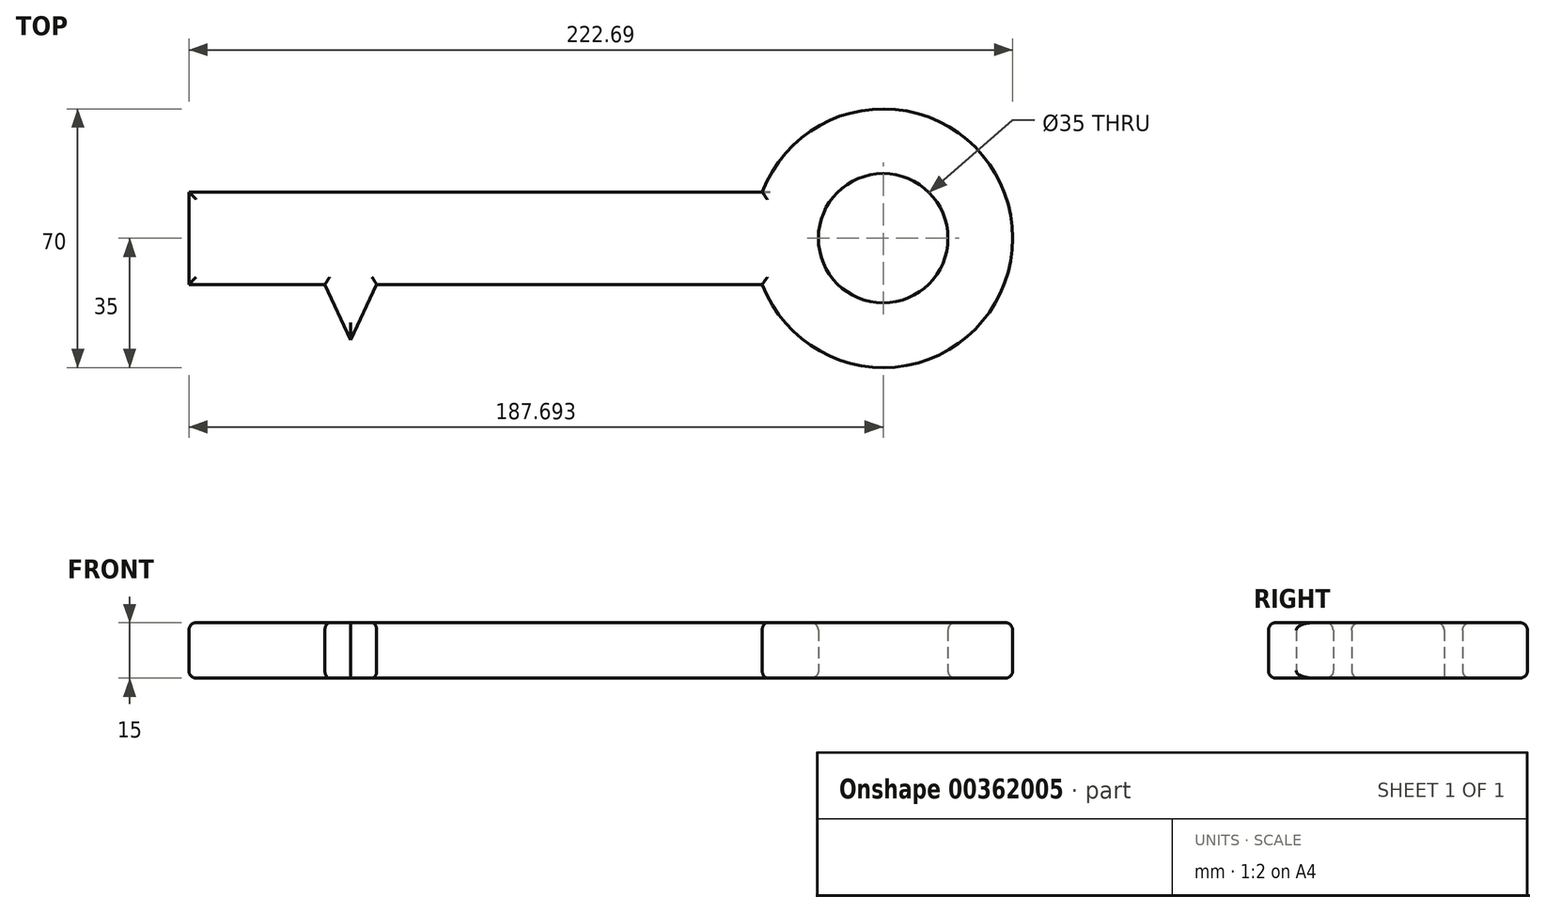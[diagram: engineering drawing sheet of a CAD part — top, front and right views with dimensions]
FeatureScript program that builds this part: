
annotation { "Feature Type Name" : "Feature", "Feature Type Description" : "" }
export const myFeature = defineFeature(function(context is Context, id is Id, definition is map)
    precondition{}
    {
        {
            var Q0;
            Q0=qCreatedBy(makeId("Top.planeOp"),FACE);
            var sketch = newSketch(context, id + "F0", { "sketchPlane" : qUnion([Q0])});
            skLineSegment(sketch, "E0.bottom", {"start": v(1.05, 45.74) * mm, "end": v(-153.95, 45.74) * mm});
            skLineSegment(sketch, "E0.top", {"start": v(1.05, 20.74) * mm, "end": v(-153.95, 20.74) * mm});
            skLineSegment(sketch, "E0.left", {"start": v(1.05, 45.74) * mm, "end": v(1.05, 20.74) * mm});
            skLineSegment(sketch, "E0.right", {"start": v(-153.95, 45.74) * mm, "end": v(-153.95, 20.74) * mm});
            skLineSegment(sketch, "E1.bottom", {"start": v(-153.95, 20.74) * mm, "end": v(-153.95, 20.74) * mm});
            skLineSegment(sketch, "E1.top", {"start": v(-153.95, -9.26) * mm, "end": v(-153.95, -9.26) * mm});
            skLineSegment(sketch, "E1.left", {"start": v(-153.95, 20.74) * mm, "end": v(-153.95, -9.26) * mm});
            skLineSegment(sketch, "E1.right", {"start": v(-153.95, 20.74) * mm, "end": v(-153.95, -9.26) * mm});
            skLineSegment(sketch, "E2.bottom", {"start": v(-153.95, -9.26) * mm, "end": v(-144.47, -9.26) * mm});
            skLineSegment(sketch, "E3.bottom", {"start": v(-144.47, -9.26) * mm, "end": v(-144.47, -9.26) * mm});
            skLineSegment(sketch, "E3.top", {"start": v(-144.47, 20.74) * mm, "end": v(-144.47, 20.74) * mm});
            skLineSegment(sketch, "E3.left", {"start": v(-144.47, -9.26) * mm, "end": v(-144.47, 20.74) * mm});
            skLineSegment(sketch, "E3.right", {"start": v(-144.47, -9.26) * mm, "end": v(-144.47, 20.74) * mm});
            skLineSegment(sketch, "E4.bottom", {"start": v(-134.47, 20.74) * mm, "end": v(-135.17, 20.74) * mm});
            skLineSegment(sketch, "E4.top", {"start": v(-134.47, 5.74) * mm, "end": v(-135.17, 5.74) * mm});
            skLineSegment(sketch, "E4.left", {"start": v(-135.17, 20.74) * mm, "end": v(-135.17, 5.74) * mm});
            skLineSegment(sketch, "E5.bottom", {"start": v(-135.17, 5.74) * mm, "end": v(-127.17, 5.74) * mm});
            skLineSegment(sketch, "E5.top", {"start": v(-135.17, 20.74) * mm, "end": v(-127.17, 20.74) * mm});
            skLineSegment(sketch, "E5.left", {"start": v(-135.17, 5.74) * mm, "end": v(-135.17, 20.74) * mm});
            skLineSegment(sketch, "E5.right", {"start": v(-127.17, 5.74) * mm, "end": v(-127.17, 20.74) * mm});
            skArc(sketch, "E6", {"start": v(1.05, 20.74) * mm, "mid": v(68.74, 33.24) * mm, "end": v(1.05, 45.74) * mm});
            skCircle(sketch, "E7", {"center": v(33.74, 33.24) * mm, "radius": 17.5 * mm});
            skLineSegment(sketch, "E8", {"start": v(-117.17, 20.74) * mm, "end": v(-110.17, 5.74) * mm});
            skLineSegment(sketch, "E9", {"start": v(-110.17, 5.74) * mm, "end": v(-103.17, 20.74) * mm});
            skSolve(sketch);
        }
        {
            var Q0;
            {var subQ0=sQuery(id+"F0.wireOp",EDGE,"E1.right");Q0=makeQuery(id+"F0.imprint","IMPRINT",FACE,{"disambiguationData":[TD([[makeQuery(id+"F0.imprint","IMPRINT",EDGE,{"derivedFrom":subQ0}),1.0]])]});}
            var Q1;
            Q1=makeQuery(id+"F0.imprint","IMPRINT",FACE,{"disambiguationData":[TD([[makeQuery(id+"F0.imprint","IMPRINT",EDGE,{"derivedFrom":sQuery(id+"F0.wireOp",EDGE,"E0.bottom")}),1.0]])]});
            var Q2;
            {var subQ0=sQuery(id+"F0.wireOp",EDGE,"E4.right");Q2=makeQuery(id+"F0.imprint","IMPRINT",FACE,{"disambiguationData":[TD([[makeQuery(id+"F0.imprint","IMPRINT",EDGE,{"derivedFrom":subQ0}),1.0]])]});}
            var Q3;
            Q3=makeQuery(id+"F0.imprint","IMPRINT",FACE,{"disambiguationData":[TD([[makeQuery(id+"F0.imprint","IMPRINT",EDGE,{"derivedFrom":sQuery(id+"F0.wireOp",EDGE,"E0.left")}),1.0]])]});
            var Q4;
            {var subQ0=sQuery(id+"F0.wireOp",EDGE,"E5.left");Q4=makeQuery(id+"F0.imprint","IMPRINT",FACE,{"disambiguationData":[TD([[makeQuery(id+"F0.imprint","IMPRINT",EDGE,{"derivedFrom":subQ0}),-1.0]])]});}
            var Q5;
            {var subQ0=sQuery(id+"F0.wireOp",EDGE,"E8");Q5=makeQuery(id+"F0.imprint","IMPRINT",FACE,{"disambiguationData":[TD([[makeQuery(id+"F0.imprint","IMPRINT",EDGE,{"derivedFrom":subQ0}),1.0]])]});}
            extrude(context, id + "F1", {"entities" : qUnion([Q0, Q1, Q2, Q3, Q4, Q5]), "depth" : 15 * mm});
        }
        {
            var Q0;
            Q0=makeQuery(id+"F1.opExtrude","CAP_EDGE",EDGE,{"disambiguationData":[OSD([sQuery(id+"F0.wireOp",EDGE,"E6")])],"isStart":true});
            var Q1;
            Q1=makeQuery(id+"F1.opExtrude","CAP_EDGE",EDGE,{"disambiguationData":[OSD([sQuery(id+"F0.wireOp",EDGE,"E7")])],"isStart":true});
            var Q2;
            {var subQ0=sQuery(id+"F0.wireOp",EDGE,"E0.top");Q2=makeQuery(id+"F1.opExtrude","CAP_EDGE",EDGE,{"disambiguationData":[OSD([subQ0]),TDD([makeQuery(id+"F0.imprint","IMPRINT",EDGE,{"disambiguationData":[TD([[makeQuery(id+"F0.imprint","INTERSECT",VERTEX,{"derivedFrom":[subQ0,sQuery(id+"F0.wireOp",EDGE,"E9")]}),1.0]])],"derivedFrom":subQ0})])],"isStart":true});}
            var Q3;
            Q3=makeQuery(id+"F1.opExtrude","CAP_EDGE",EDGE,{"disambiguationData":[OSD([sQuery(id+"F0.wireOp",EDGE,"E9")])],"isStart":true});
            var Q4;
            Q4=makeQuery(id+"F1.opExtrude","CAP_EDGE",EDGE,{"disambiguationData":[OSD([sQuery(id+"F0.wireOp",EDGE,"E5.right")])],"isStart":true});
            var Q5;
            {var subQ0=sQuery(id+"F0.wireOp",EDGE,"E0.top");Q5=makeQuery(id+"F1.opExtrude","CAP_EDGE",EDGE,{"disambiguationData":[OSD([subQ0]),TDD([makeQuery(id+"F0.imprint","IMPRINT",EDGE,{"disambiguationData":[TD([[makeQuery(id+"F0.imprint","INTERSECT",VERTEX,{"derivedFrom":[subQ0,sQuery(id+"F0.wireOp",EDGE,"E8")]}),-1.0]])],"derivedFrom":subQ0})])],"isStart":true});}
            var Q6;
            Q6=makeQuery(id+"F1.opExtrude","CAP_EDGE",EDGE,{"disambiguationData":[OSD([sQuery(id+"F0.wireOp",EDGE,"E8")])],"isStart":true});
            var Q7;
            Q7=makeQuery(id+"F1.opExtrude","CAP_EDGE",EDGE,{"disambiguationData":[OSD([sQuery(id+"F0.wireOp",EDGE,"E5.left")])],"isStart":true});
            var Q8;
            Q8=makeQuery(id+"F1.opExtrude","CAP_EDGE",EDGE,{"disambiguationData":[OSD([sQuery(id+"F0.wireOp",EDGE,"E5.bottom")])],"isStart":true});
            var Q9;
            {var subQ0=sQuery(id+"F0.wireOp",EDGE,"E0.top");Q9=makeQuery(id+"F1.opExtrude","CAP_EDGE",EDGE,{"disambiguationData":[OSD([subQ0]),TDD([makeQuery(id+"F0.imprint","IMPRINT",EDGE,{"disambiguationData":[TD([[makeQuery(id+"F0.imprint","INTERSECT",VERTEX,{"derivedFrom":[subQ0,sQuery(id+"F0.wireOp",EDGE,"E3.right")]}),1.0]])],"derivedFrom":subQ0})])],"isStart":true});}
            var Q10;
            Q10=makeQuery(id+"F1.opExtrude","CAP_EDGE",EDGE,{"disambiguationData":[OSD([sQuery(id+"F0.wireOp",EDGE,"E3.right")])],"isStart":true});
            var Q11;
            Q11=makeQuery(id+"F1.opExtrude","CAP_EDGE",EDGE,{"disambiguationData":[OSD([sQuery(id+"F0.wireOp",EDGE,"E2.bottom")])],"isStart":true});
            var Q12;
            Q12=makeQuery(id+"F1.opExtrude","CAP_EDGE",EDGE,{"disambiguationData":[OSD([sQuery(id+"F0.wireOp",EDGE,"E0.right"),sQuery(id+"F0.wireOp",EDGE,"E1.right")])],"isStart":true});
            fillet(context, id + "F2", {"entities" : qUnion([Q0, Q1, Q2, Q3, Q4, Q5, Q6, Q7, Q8, Q9, Q10, Q11, Q12]), "radius" : 2 * mm, "tangentPropagation" : true, "allowEdgeOverflow" : false});
        }
        {
            var Q0;
            Q0=makeQuery(id+"F1.opExtrude","CAP_FACE",FACE,{"disambiguationData":[OSD([sQuery(id+"F0.wireOp",EDGE,"E0.bottom"),sQuery(id+"F0.wireOp",EDGE,"E0.top"),sQuery(id+"F0.wireOp",EDGE,"E0.right"),sQuery(id+"F0.wireOp",EDGE,"E1.right"),sQuery(id+"F0.wireOp",EDGE,"E2.bottom"),sQuery(id+"F0.wireOp",EDGE,"E3.right"),sQuery(id+"F0.wireOp",EDGE,"E5.bottom"),sQuery(id+"F0.wireOp",EDGE,"E5.left"),sQuery(id+"F0.wireOp",EDGE,"E5.right"),sQuery(id+"F0.wireOp",EDGE,"E6"),sQuery(id+"F0.wireOp",EDGE,"E7"),sQuery(id+"F0.wireOp",EDGE,"E8"),sQuery(id+"F0.wireOp",EDGE,"E9")])],"isStart":false});
            fillet(context, id + "F3", {"entities" : qUnion([Q0]), "radius" : 2 * mm, "tangentPropagation" : true, "allowEdgeOverflow" : false});
        }
    });
